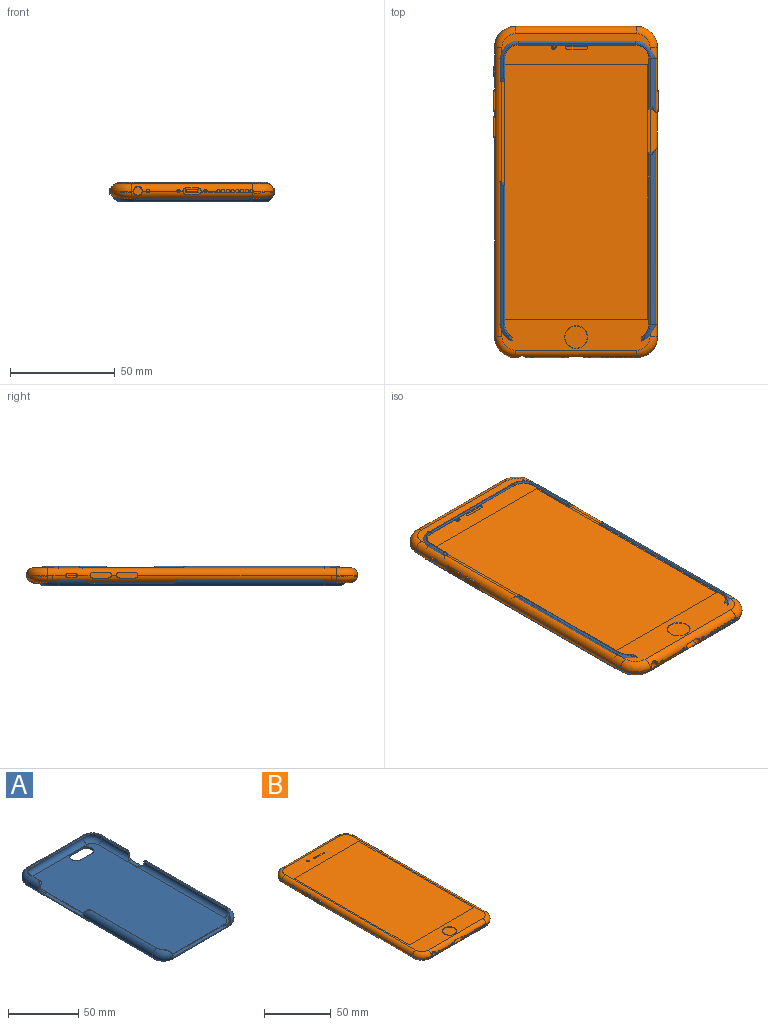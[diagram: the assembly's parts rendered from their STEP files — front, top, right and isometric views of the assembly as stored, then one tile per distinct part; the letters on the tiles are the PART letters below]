
ASSEMBLY  parts=2 mates=1
PART A: 91 faces, bbox 79x150.1x9.5 mm
  f0: cylinder r=3.5mm len=127.1mm, axis (0,1,0), area 1149.3mm2, adj f1,f8,f14,f16,f26,f53,f54,f55
  f1: cylinder r=0.5mm len=82.87mm, axis (0,1,0), area 128mm2, adj f0,f9,f15,f59,f60
  f2: cylinder r=3.5mm len=127.1mm, axis (0,1,0), area 873.9mm2, adj f3,f5,f11,f22,f26,f27,f28,f42
  f3: cylinder r=0.5mm len=11.42mm, axis (0,1,0), area 15.6mm2, adj f2,f4,f23,f46,f51
  f4: cylinder r=5mm len=127.1mm, axis (0,1,0), area 1097.8mm2, adj f3,f13,f24,f25,f27,f51,f52,f84
  f5: plane 16.43x0mm, normal (1,0,0), area 0.1mm2, adj f2,f26,f42
  f6: cylinder r=3.5mm len=56mm, axis (1,0,0), area 26.2mm2, adj f8,f11,f26,f31,f34,f35,f40,f41
  f7: cylinder r=5mm len=56mm, axis (1,0,0), area 114.5mm2, adj f10,f13,f25,f71,f72,f73
  f8: torus R=5.74mm, axis (0,0,1), area 122.4mm2, adj f0,f6,f9,f26,f29,f30,f31
  f9: torus R=6.88mm, axis (0,0,1), area 10.2mm2, adj f1,f8,f10,f29,f32,f33
  f10: torus R=5.6mm, axis (0,0,1), area 165.3mm2, adj f7,f9,f15,f25,f32,f74,f75,f76
  f11: torus R=5.74mm, axis (0,0,1), area 122.4mm2, adj f2,f6,f12,f26,f35,f36,f37
  f12: torus R=6.88mm, axis (0,0,1), area 10.2mm2, adj f11,f13,f27,f37,f38,f39
  f13: torus R=5.6mm, axis (0,0,1), area 165.3mm2, adj f4,f7,f12,f25,f38,f68,f69,f70
  f14: cylinder r=0.5mm len=24.73mm, axis (0,1,0), area 36.6mm2, adj f0,f15,f17,f53,f61
  f15: cylinder r=5mm len=127.1mm, axis (0,1,0), area 1384.9mm2, adj f1,f10,f14,f18,f25,f60,f61,f77
  f16: torus R=5.74mm, axis (0,0,1), area 129.9mm2, adj f0,f17,f19,f26
  f17: torus R=6.88mm, axis (0,0,1), area 16.2mm2, adj f14,f16,f18,f20
  f18: torus R=5.6mm, axis (0,0,1), area 182mm2, adj f15,f17,f21,f25
  f19: cylinder r=3.5mm len=56mm, axis (-1,0,0), area 572.6mm2, adj f16,f20,f22,f26,f64
  f20: cylinder r=0.5mm len=56mm, axis (-1,0,0), area 88mm2, adj f17,f19,f21,f23
  f21: cylinder r=5mm len=56mm, axis (-1,0,0), area 688.9mm2, adj f18,f20,f24,f25
  f22: torus R=5.74mm, axis (0,0,1), area 129.9mm2, adj f2,f19,f23,f26
  f23: torus R=6.88mm, axis (0,0,1), area 16.2mm2, adj f3,f20,f22,f24
  f24: torus R=5.6mm, axis (0,0,1), area 182mm2, adj f4,f21,f23,f25
  f25: plane 142.1x71mm, normal (0,0,-1), area 9861.1mm2, adj f4,f7,f10,f13,f15,f18,f21,f24
  f26: plane 138.18x67.14mm, normal (0,0,1), area 9053.4mm2, adj f0,f2,f5,f6,f8,f11,f16,f19
  f27: cylinder r=0.5mm len=68.7mm, axis (0,1,0), area 105.6mm2, adj f2,f4,f12,f47,f52
  f28: plane 73.67x0mm, normal (1,0,0), area 0.3mm2, adj f2,f26,f43
  f29: cylinder r=3.5mm len=4.97mm, axis (0,1,0), area 7.4mm2, adj f8,f9,f30,f32,f33,f76
  f30: plane 1.06x0.55mm, normal (-1,0,0), area 0.5mm2, adj f8,f29,f31,f75
  f31: cylinder r=3.5mm len=4.29mm, axis (0,1,0), area 9.6mm2, adj f6,f8,f30,f34,f73,f74
  f32: plane 1.34x0.37mm, normal (-1,0,0), area 0.2mm2, adj f9,f10,f29,f33,f76
  f33: plane 0.66x0.4mm, normal (0,-1,0), area 0.1mm2, adj f9,f29,f32
  f34: plane 50.8x3.01mm, normal (0,0,1), area 152.9mm2, adj f6,f31,f35,f72
  f35: cylinder r=3.5mm len=4.29mm, axis (0,1,0), area 9.6mm2, adj f6,f11,f34,f36,f70,f71
  f36: plane 1.06x0.55mm, normal (1,0,0), area 0.5mm2, adj f11,f35,f37,f69
  f37: cylinder r=3.5mm len=4.97mm, axis (0,1,0), area 7.4mm2, adj f11,f12,f36,f38,f39,f68
  f38: plane 1.34x0.37mm, normal (1,0,0), area 0.2mm2, adj f12,f13,f37,f39,f68
  f39: plane 0.66x0.4mm, normal (0,-1,0), area 0.1mm2, adj f12,f37,f38
  f40: cylinder r=3.5mm len=0.17mm, axis (0,1,0), area 0mm2, adj f6,f26
  f41: cylinder r=3.5mm len=0.17mm, axis (0,1,0), area 0mm2, adj f6,f26
  f42: cylinder r=3.5mm len=0.17mm, axis (-1,0,0), area 0mm2, adj f2,f5,f26
  f43: cylinder r=3.5mm len=0.17mm, axis (-1,0,0), area 0mm2, adj f2,f26,f28
  f44: plane 37x3.01mm, normal (0,0,1), area 111.4mm2, adj f2,f49,f50,f87
  f45: plane 1.06x0.47mm, normal (0,-1,0), area 0.5mm2, adj f2,f46,f49,f89
  f46: cylinder r=3.5mm len=3.8mm, axis (-1,0,0), area 8.6mm2, adj f2,f3,f45,f51,f90
  f47: cylinder r=3.5mm len=3.8mm, axis (-1,0,0), area 8.6mm2, adj f2,f27,f48,f52,f84
  f48: plane 1.09x0.97mm, normal (0,1,0), area 1mm2, adj f2,f47,f50,f85
  f49: cylinder r=3.5mm len=4.36mm, axis (-1,0,0), area 8.9mm2, adj f2,f44,f45,f88
  f50: cylinder r=3.5mm len=4.38mm, axis (-1,0,0), area 10.2mm2, adj f2,f44,f48,f86
  f51: plane 1.53x0.39mm, normal (0,-1,0), area 0.3mm2, adj f3,f4,f46,f90
  f52: plane 1.53x0.39mm, normal (0,1,0), area 0.3mm2, adj f4,f27,f47,f84
  f53: cylinder r=3.5mm len=3.85mm, axis (1,0,0), area 9mm2, adj f0,f14,f54,f61,f77
  f54: plane 1.05x0.32mm, normal (0,-1,0), area 0.3mm2, adj f0,f53,f55,f78
  f55: cylinder r=3.5mm len=4.36mm, axis (1,0,0), area 8.9mm2, adj f0,f54,f56,f79
  f56: plane 9x3.01mm, normal (0,0,1), area 27.1mm2, adj f0,f55,f57,f80
  f57: cylinder r=3.5mm len=4.36mm, axis (1,0,0), area 8.9mm2, adj f0,f56,f58,f81
  f58: plane 1.05x0.32mm, normal (0,1,0), area 0.3mm2, adj f0,f57,f59,f82
  f59: cylinder r=3.5mm len=3.85mm, axis (1,0,0), area 9mm2, adj f0,f1,f58,f60,f83
  f60: plane 1.84x0.56mm, normal (0,1,0), area 0.6mm2, adj f1,f15,f59,f83
  f61: plane 1.84x0.56mm, normal (0,-1,0), area 0.6mm2, adj f14,f15,f53,f77
  f62: cylinder r=3.5mm len=0.17mm, axis (1,0,0), area 0mm2, adj f0,f26
  f63: cylinder r=3.5mm len=0.17mm, axis (1,0,0), area 0mm2, adj f0,f26
  f64: plane 10.12x1.61mm, normal (0,-1,0), area 16.2mm2, adj f19,f25,f65,f67
  f65: cylinder r=5mm len=10mm, axis (0,0,1), area 25.1mm2, adj f25,f26,f64,f66
  f66: plane 10.11x1.6mm, normal (0,1,0), area 16.2mm2, adj f25,f26,f65,f67
  f67: cylinder r=5mm len=10mm, axis (0,0,1), area 25.1mm2, adj f25,f26,f64,f66
  f68: bspline ~4.29x3.86mm, area 2.1mm2, adj f13,f37,f38,f69
  f69: bspline ~0.6x0.38mm, area 0.2mm2, adj f13,f36,f68,f70
  f70: bspline ~2.94x1.44mm, area 1.4mm2, adj f13,f35,f69,f71
  f71: bspline ~2.6x1.46mm, area 1.5mm2, adj f7,f35,f70,f72
  f72: plane 50.8x0.51mm, normal (0,-0.92,0.38), area 28mm2, adj f7,f34,f71,f73
  f73: bspline ~2.6x1.46mm, area 1.5mm2, adj f7,f31,f72,f74
  f74: bspline ~2.94x1.45mm, area 1.4mm2, adj f10,f31,f73,f75
  f75: bspline ~0.6x0.38mm, area 0.2mm2, adj f10,f30,f74,f76
  f76: bspline ~4.29x3.86mm, area 2.1mm2, adj f10,f29,f32,f75
  f77: bspline ~3.8x3.54mm, area 1.8mm2, adj f15,f53,f61,f78
  f78: cone r=4.7mm half-angle=45deg, axis (0,1,0), area 0.1mm2, adj f15,f54,f77,f79
  f79: bspline ~4.04x3.8mm, area 2.9mm2, adj f15,f55,f78,f80
  f80: plane 9x0.51mm, normal (0.92,0,0.38), area 5mm2, adj f15,f56,f79,f81
  f81: bspline ~4.04x3.8mm, area 2.9mm2, adj f15,f57,f80,f82
  f82: cone r=4.7mm half-angle=45deg, axis (0,-1,0), area 0.1mm2, adj f15,f58,f81,f83
  f83: bspline ~3.5x3.5mm, area 1.8mm2, adj f15,f59,f60,f82
  f84: bspline ~3.81x3.54mm, area 1.7mm2, adj f4,f47,f52,f85
  f85: cone r=5mm half-angle=45deg, axis (0,-1,0), area 0.4mm2, adj f4,f48,f84,f86
  f86: bspline ~3.79x3.79mm, area 2.7mm2, adj f4,f50,f85,f87
  f87: plane 37x0.51mm, normal (-0.92,0,0.38), area 20.4mm2, adj f4,f44,f86,f88
  f88: bspline ~4.04x3.8mm, area 2.9mm2, adj f4,f49,f87,f89
  f89: cone r=5mm half-angle=45deg, axis (0,1,0), area 0.2mm2, adj f4,f45,f88,f90
  f90: bspline ~3.81x3.54mm, area 1.7mm2, adj f4,f46,f51,f89
PART B: 184 faces, bbox 79.4x159.7x7.8 mm
  f0: cylinder r=3.55mm len=3.55mm, axis (0,1,0), area 12.2mm2, adj f2,f5,f6,f32,f62
  f1: cylinder r=3.55mm len=3.55mm, axis (0,-1,0), area 12.2mm2, adj f2,f4,f7,f36,f59
  f2: plane 70.69x1.5mm, normal (0,0,-1), area 106mm2, adj f0,f1,f8,f39
  f3: cylinder r=3.55mm len=57.79mm, axis (-1,0,0), area 154.9mm2, adj f4,f5,f9,f10,f11,f12,f13,f14
  f4: torus R=6.45mm, axis (0,0,-1), area 41.5mm2, adj f1,f3,f22,f23,f49,f50
  f5: torus R=6.45mm, axis (0,0,-1), area 42.1mm2, adj f0,f3,f24,f25,f69
  f6: cylinder r=3.55mm len=132.83mm, axis (0,1,0), area 710.8mm2, adj f0,f8,f28,f62,f78,f79,f81,f83
  f7: cylinder r=3.55mm len=132.83mm, axis (0,-1,0), area 709.9mm2, adj f1,f8,f27,f59,f74,f99,f100,f101
  f8: plane 132.83x70.69mm, normal (0,0,-1), area 9132.5mm2, adj f2,f6,f7,f26,f48,f65
  f9: cylinder r=3.55mm len=0.95mm, axis (-1,0,0), area 0.1mm2, adj f3,f43,f148
  f10: cylinder r=3.55mm len=2mm, axis (-1,0,0), area 0.4mm2, adj f3,f43,f56,f148
  f11: cylinder r=3.55mm len=13.09mm, axis (-1,0,0), area 4.2mm2, adj f3,f40,f43,f56
  f12: cylinder r=3.55mm len=1.41mm, axis (-1,0,0), area 0.5mm2, adj f3,f40,f43,f109
  f13: cylinder r=3.55mm len=1.49mm, axis (-1,0,0), area 0.7mm2, adj f3,f43,f44,f111
  f14: cylinder r=3.55mm len=5.01mm, axis (-1,0,0), area 2.5mm2, adj f3,f43,f44,f131
  f15: cylinder r=3.55mm len=1.06mm, axis (-1,0,0), area 0.5mm2, adj f3,f43,f129,f131
  f16: cylinder r=3.55mm len=1.09mm, axis (-1,0,0), area 0.5mm2, adj f3,f43,f127,f129
  f17: cylinder r=3.55mm len=1.12mm, axis (-1,0,0), area 0.5mm2, adj f3,f43,f125,f127
  f18: cylinder r=3.55mm len=1.14mm, axis (-1,0,0), area 0.5mm2, adj f3,f43,f123,f125
  f19: cylinder r=3.55mm len=1.17mm, axis (-1,0,0), area 0.5mm2, adj f3,f43,f121,f123
  f20: cylinder r=3.55mm len=1.2mm, axis (-1,0,0), area 0.6mm2, adj f3,f43,f119,f121
  f21: cylinder r=3.55mm len=1.23mm, axis (-1,0,0), area 0.6mm2, adj f3,f43,f117,f119
  f22: torus R=6.45mm, axis (0,0,-1), area 4.3mm2, adj f4,f50
  f23: torus R=6.45mm, axis (0,0,-1), area 5.8mm2, adj f4,f50,f117
  f24: torus R=6.45mm, axis (0,0,-1), area 4.7mm2, adj f5,f72
  f25: torus R=6.45mm, axis (0,0,-1), area 4.7mm2, adj f5,f72
  f26: plane 70.69x1.5mm, normal (0,0,-1), area 106mm2, adj f8,f27,f28,f47
  f27: cylinder r=3.55mm len=3.55mm, axis (0,-1,0), area 12.2mm2, adj f7,f26,f31,f58,f59
  f28: cylinder r=3.55mm len=3.55mm, axis (0,1,0), area 12.1mm2, adj f6,f26,f29,f33,f61,f62
  f29: torus R=6.45mm, axis (0,0,-1), area 42.4mm2, adj f28,f30,f34,f35,f66,f67
  f30: cylinder r=3.55mm len=57.79mm, axis (1,0,0), area 196mm2, adj f29,f31,f68,f70
  f31: torus R=6.45mm, axis (0,0,-1), area 42.1mm2, adj f27,f30,f37,f38,f71
  f32: cylinder r=3.55mm len=2.05mm, axis (0,1,0), area 2.4mm2, adj f0,f39,f69
  f33: cylinder r=3.55mm len=0.28mm, axis (0,1,0), area 0mm2, adj f28,f34,f62
  f34: torus R=6.45mm, axis (0,0,-1), area 3.4mm2, adj f29,f33,f67
  f35: torus R=6.45mm, axis (0,0,-1), area 5.7mm2, adj f29,f67
  f36: cylinder r=3.55mm len=2.05mm, axis (0,-1,0), area 2.4mm2, adj f1,f39,f49
  f37: torus R=6.45mm, axis (0,0,-1), area 4.7mm2, adj f31,f73
  f38: torus R=6.45mm, axis (0,0,-1), area 4.7mm2, adj f31,f73
  f39: plane 70.69x7.57mm, normal (0,0,-1), area 517.3mm2, adj f2,f32,f36,f42,f49,f69
  f40: cylinder r=3.55mm len=1.6mm, axis (-1,0,0), area 0.8mm2, adj f3,f11,f12,f41,f168,f169,f170,f171
  f41: cylinder r=3.55mm len=1.6mm, axis (1,0,0), area 0.9mm2, adj f40,f43,f163,f164,f165,f166,f167,f168
  f42: cylinder r=3.55mm len=57.79mm, axis (-1,0,0), area 124.3mm2, adj f3,f39,f49,f69
  f43: cylinder r=3.55mm len=57.79mm, axis (1,0,0), area 290.7mm2, adj f9,f10,f11,f12,f13,f14,f15,f16
  f44: cylinder r=3.55mm len=1.6mm, axis (-1,0,0), area 0.8mm2, adj f3,f13,f14,f45,f153,f154,f155,f156
  f45: cylinder r=3.55mm len=1.6mm, axis (1,0,0), area 0.9mm2, adj f43,f44,f150,f151,f152,f153,f159,f160
  f46: plane 1.5x1.5mm, normal (0,0,1), area 1mm2, adj f142,f143
  f47: plane 70.69x7.57mm, normal (0,0,-1), area 456.1mm2, adj f26,f58,f61,f66,f68,f71,f104,f144
  f48: plane 18.21x17.51mm, normal (0,0,-1), area 242.8mm2, adj f8
  f49: torus R=6.45mm, axis (0,0,-1), area 24.6mm2, adj f4,f36,f39,f42
  f50: torus R=6.45mm, axis (0,0,-1), area 76.2mm2, adj f4,f22,f23,f43,f59,f63,f117
  f51: cylinder r=1.7mm len=1.7mm, axis (0,0,-1), area 1.5mm2, adj f52,f54,f113
  f52: cylinder r=1.7mm len=6.5mm, axis (1,0,0), area 10.1mm2, adj f51,f53,f54,f114
  f53: cylinder r=1.7mm len=1.7mm, axis (0,0,1), area 1.5mm2, adj f52,f54,f115
  f54: cylinder r=1.7mm len=6.5mm, axis (-1,0,0), area 10.1mm2, adj f51,f52,f53,f116
  f55: plane 8.7x2.95mm, normal (0,-1,0), area 12.7mm2, adj f109,f110,f111,f112,f113,f114,f115,f116
  f56: cylinder r=3.55mm len=1.6mm, axis (-1,0,0), area 1mm2, adj f3,f10,f11,f57
  f57: cylinder r=3.55mm len=1.6mm, axis (1,0,0), area 1mm2, adj f43,f56
  f58: cylinder r=3.55mm len=2.05mm, axis (0,-1,0), area 2.4mm2, adj f27,f47,f71
  f59: cylinder r=3.55mm len=138.07mm, axis (0,1,0), area 739.1mm2, adj f1,f7,f27,f50,f63,f73,f75,f98
  f60: plane 5.61x1.96mm, normal (-1,0,0), area 5.5mm2, adj f88,f89,f90,f91,f92,f93,f94,f95
  f61: cylinder r=3.55mm len=2.09mm, axis (0,1,0), area 2.5mm2, adj f28,f47,f66
  f62: cylinder r=3.55mm len=138.07mm, axis (0,-1,0), area 737.2mm2, adj f0,f6,f28,f33,f63,f67,f72,f79
  f63: plane 150.97x70.69mm, normal (0,0,1), area 2217.1mm2, adj f43,f50,f59,f62,f64,f67,f70,f72
  f64: plane 121.54x68.36mm, normal (0,0,1), area 8308.5mm2, adj f63
  f65: plane 5.18x4.88mm, normal (0,0,-1), area 13.6mm2, adj f8
  f66: torus R=6.45mm, axis (0,0,-1), area 24.8mm2, adj f29,f47,f61,f68
  f67: torus R=6.45mm, axis (0,0,-1), area 76.3mm2, adj f29,f34,f35,f62,f63,f70
  f68: cylinder r=3.55mm len=57.79mm, axis (1,0,0), area 126.3mm2, adj f30,f47,f66,f71,f106
  f69: torus R=6.45mm, axis (0,0,-1), area 24.8mm2, adj f5,f32,f39,f42
  f70: cylinder r=3.55mm len=57.79mm, axis (-1,0,0), area 322.3mm2, adj f30,f63,f67,f73
  f71: torus R=6.45mm, axis (0,0,-1), area 24.8mm2, adj f31,f47,f58,f68
  f72: torus R=6.45mm, axis (0,0,-1), area 76.3mm2, adj f24,f25,f43,f62,f63
  f73: torus R=6.45mm, axis (0,0,-1), area 76.3mm2, adj f37,f38,f59,f63,f70
  f74: cylinder r=3.55mm len=15.81mm, axis (0,-1,0), area 17.2mm2, adj f7,f75,f102
  f75: cylinder r=3.55mm len=15.81mm, axis (0,1,0), area 16.6mm2, adj f59,f74,f102
  f76: cone r=5.45mm half-angle=45deg, axis (0,0,1), area 7.2mm2, adj f63,f77
  f77: plane 10.6x10.6mm, normal (0,0,1), area 88.2mm2, adj f76
  f78: plane 7.4x0.59mm, normal (0,0,-1), area 4.3mm2, adj f6,f79,f81,f82
  f79: cylinder r=1.4mm len=2.8mm, axis (-1,0,0), area 2mm2, adj f6,f62,f78,f80,f82
  f80: plane 7.4x0.59mm, normal (0,0,1), area 4.3mm2, adj f62,f79,f81,f82
  f81: cylinder r=1.4mm len=2.8mm, axis (-1,0,0), area 2mm2, adj f6,f62,f78,f80,f82
  f82: plane 10.2x2.8mm, normal (-1,0,0), area 26.9mm2, adj f78,f79,f80,f81
  f83: plane 7.4x0.59mm, normal (0,0,-1), area 4.3mm2, adj f6,f84,f86,f87
  f84: cylinder r=1.4mm len=2.8mm, axis (-1,0,0), area 2mm2, adj f6,f62,f83,f85,f87
  f85: plane 7.4x0.59mm, normal (0,0,1), area 4.3mm2, adj f62,f84,f86,f87
  f86: cylinder r=1.4mm len=2.8mm, axis (-1,0,0), area 2mm2, adj f6,f62,f83,f85,f87
  f87: plane 10.2x2.8mm, normal (-1,0,0), area 26.9mm2, adj f83,f84,f85,f86
  f88: cylinder r=0.98mm len=1.96mm, axis (-1,0,0), area 1.3mm2, adj f6,f60,f62,f89,f91
  f89: plane 3.65x0.36mm, normal (0,0,-1), area 1.3mm2, adj f60,f62,f88,f90
  f90: cylinder r=0.98mm len=1.96mm, axis (-1,0,0), area 1.3mm2, adj f6,f60,f62,f89,f91
  f91: plane 3.65x0.36mm, normal (0,0,1), area 1.3mm2, adj f6,f60,f88,f90
  f92: cylinder r=0.47mm len=0.93mm, axis (1,0,0), area 1.2mm2, adj f60,f93,f95,f96
  f93: plane 4.31x0.8mm, normal (0,0,-1), area 3.4mm2, adj f60,f92,f94,f96
  f94: cylinder r=0.47mm len=0.93mm, axis (1,0,0), area 1.2mm2, adj f60,f93,f95,f96
  f95: plane 4.31x0.8mm, normal (0,0,1), area 3.4mm2, adj f60,f92,f94,f96
  f96: plane 5.24x0.93mm, normal (-1,0,0), area 4.7mm2, adj f92,f93,f94,f95
  f97: plane 10.2x2.8mm, normal (1,0,0), area 26.9mm2, adj f98,f99,f100,f101
  f98: plane 7.4x0.59mm, normal (0,0,1), area 4.3mm2, adj f59,f97,f99,f101
  f99: cylinder r=1.4mm len=2.8mm, axis (1,0,0), area 2mm2, adj f7,f59,f97,f98,f100
  f100: plane 7.4x0.59mm, normal (0,0,-1), area 4.3mm2, adj f7,f97,f99,f101
  f101: cylinder r=1.4mm len=2.8mm, axis (1,0,0), area 2mm2, adj f7,f59,f97,f98,f100
  f102: cylinder r=1mm len=2mm, axis (1,0,0), area 7.3mm2, adj f74,f75,f103
  f103: plane 2x2mm, normal (1,0,0), area 3.1mm2, adj f102
  f104: cylinder r=3.83mm len=7.66mm, axis (0,0,1), area 16.1mm2, adj f47,f105,f106
  f105: plane 7.66x7.66mm, normal (0,0,-1), area 46.1mm2, adj f104
  f106: plane 2.32x0.18mm, normal (0,0,1), area 0.3mm2, adj f68,f104
  f107: cylinder r=2.02mm len=9.64mm, axis (0,-1,0), area 117.8mm2, adj f108,f148,f149
  f108: plane 4.05x4.05mm, normal (0,-1,0), area 12.9mm2, adj f107
  f109: cylinder r=1.47mm len=5mm, axis (0,-1,0), area 22.5mm2, adj f3,f12,f43,f55,f110,f112
  f110: plane 5.75x4.68mm, normal (0,0,-1), area 26.9mm2, adj f43,f55,f109,f111
  f111: cylinder r=1.47mm len=5mm, axis (0,-1,0), area 22.5mm2, adj f3,f13,f43,f55,f110,f112
  f112: plane 5.75x4.68mm, normal (0,0,1), area 26.9mm2, adj f3,f55,f109,f111
  f113: plane 1.7x0.8mm, normal (1,0,0), area 1.4mm2, adj f51,f55,f114,f116
  f114: plane 6.5x0.8mm, normal (0,0,1), area 5.2mm2, adj f52,f55,f113,f115
  f115: plane 1.7x0.8mm, normal (-1,0,0), area 1.4mm2, adj f53,f55,f114,f116
  f116: plane 6.5x0.8mm, normal (0,0,-1), area 5.2mm2, adj f54,f55,f113,f115
  f117: cylinder r=0.8mm len=1.6mm, axis (0,-1,0), area 4.9mm2, adj f3,f21,f23,f43,f50,f118
  f118: plane 1.6x1.6mm, normal (0,-1,0), area 2mm2, adj f117
  f119: cylinder r=0.8mm len=1.6mm, axis (0,-1,0), area 4.9mm2, adj f3,f20,f21,f43,f120
  f120: plane 1.6x1.6mm, normal (0,-1,0), area 2mm2, adj f119
  f121: cylinder r=0.8mm len=1.6mm, axis (0,-1,0), area 4.9mm2, adj f3,f19,f20,f43,f122
  f122: plane 1.6x1.6mm, normal (0,-1,0), area 2mm2, adj f121
  f123: cylinder r=0.8mm len=1.6mm, axis (0,-1,0), area 4.9mm2, adj f3,f18,f19,f43,f124
  f124: plane 1.6x1.6mm, normal (0,-1,0), area 2mm2, adj f123
  f125: cylinder r=0.8mm len=1.6mm, axis (0,-1,0), area 4.9mm2, adj f3,f17,f18,f43,f126
  f126: plane 1.6x1.6mm, normal (0,-1,0), area 2mm2, adj f125
  f127: cylinder r=0.8mm len=1.6mm, axis (0,-1,0), area 4.9mm2, adj f3,f16,f17,f43,f128
  f128: plane 1.6x1.6mm, normal (0,-1,0), area 2mm2, adj f127
  f129: cylinder r=0.8mm len=1.6mm, axis (0,-1,0), area 4.9mm2, adj f3,f15,f16,f43,f130
  f130: plane 1.6x1.6mm, normal (0,-1,0), area 2mm2, adj f129
  f131: cylinder r=0.8mm len=1.6mm, axis (0,-1,0), area 4.9mm2, adj f3,f14,f15,f43,f132
  f132: plane 1.6x1.6mm, normal (0,-1,0), area 2mm2, adj f131
  f133: cylinder r=0.6mm len=1.2mm, axis (0,0,1), area 0.2mm2, adj f63,f134,f136,f137
  f134: plane 9.5x0.1mm, normal (0,-1,0), area 1mm2, adj f63,f133,f135,f137
  f135: cylinder r=0.6mm len=1.2mm, axis (0,0,1), area 0.2mm2, adj f63,f134,f136,f137
  f136: plane 9.5x0.1mm, normal (0,1,0), area 1mm2, adj f63,f133,f135,f137
  f137: plane 10.7x1.2mm, normal (0,0,1), area 12.5mm2, adj f133,f134,f135,f136
  f138: cylinder r=1.25mm len=2.5mm, axis (0,0,1), area 2mm2, adj f63,f139
  f139: plane 2.5x2.5mm, normal (0,0,1), area 1.8mm2, adj f138,f140
  f140: cylinder r=1mm len=2mm, axis (0,0,1), area 1.6mm2, adj f139,f141
  f141: plane 2x2mm, normal (0,0,1), area 1.4mm2, adj f140,f142
  f142: cylinder r=0.75mm len=1.5mm, axis (0,0,1), area 1.2mm2, adj f46,f141
  f143: sphere r=0.5mm, area 1.6mm2, adj f46
  f144: cylinder r=2.06mm len=4.11mm, axis (0,0,1), area 0.6mm2, adj f47,f145
  f145: plane 4.11x4.11mm, normal (0,0,-1), area 13.3mm2, adj f144
  f146: cylinder r=0.8mm len=1.6mm, axis (0,0,-1), area 0.5mm2, adj f47,f147
  f147: plane 1.6x1.6mm, normal (0,0,-1), area 2mm2, adj f146
  f148: bspline ~4.23x2.35mm, area 2.8mm2, adj f3,f9,f10,f107,f149
  f149: bspline ~4.23x2.35mm, area 2.8mm2, adj f43,f107,f148
  f150: plane 0.2x0.17mm, normal (0,0,-1), area 0mm2, adj f45,f151,f161,f162
  f151: plane 0.35x0.2mm, normal (-1,0,0), area 0.1mm2, adj f45,f150,f152,f162
  f152: plane 0.35x0.2mm, normal (0,0,-1), area 0.1mm2, adj f45,f151,f153,f162
  f153: plane 0.2x0.2mm, normal (-1,0,0), area 0mm2, adj f44,f45,f152,f154,f162
  f154: plane 0.35x0.2mm, normal (0,0,1), area 0.1mm2, adj f44,f153,f155,f162
  f155: plane 0.35x0.2mm, normal (-1,0,0), area 0.1mm2, adj f44,f154,f156,f162
  f156: plane 0.2x0.17mm, normal (0,0,1), area 0mm2, adj f44,f155,f157,f162
  f157: plane 0.35x0.2mm, normal (1,0,0), area 0.1mm2, adj f44,f156,f158,f162
  f158: plane 0.35x0.2mm, normal (0,0,1), area 0.1mm2, adj f44,f157,f159,f162
  f159: plane 0.2x0.2mm, normal (1,0,0), area 0mm2, adj f44,f45,f158,f160,f162
  f160: plane 0.35x0.2mm, normal (0,0,-1), area 0.1mm2, adj f45,f159,f161,f162
  f161: plane 0.35x0.2mm, normal (1,0,0), area 0.1mm2, adj f45,f150,f160,f162
  f162: plane 0.9x0.9mm, normal (0,-1,0), area 0.3mm2, adj f150,f151,f152,f153,f154,f155,f156,f157
  f163: plane 0.35x0.2mm, normal (0,0,-1), area 0.1mm2, adj f41,f164,f174,f175
  f164: plane 0.35x0.2mm, normal (-1,0,0), area 0.1mm2, adj f41,f163,f165,f175
  f165: plane 0.2x0.17mm, normal (0,0,-1), area 0mm2, adj f41,f164,f166,f175
  f166: plane 0.35x0.2mm, normal (1,0,0), area 0.1mm2, adj f41,f165,f167,f175
  f167: plane 0.35x0.2mm, normal (0,0,-1), area 0.1mm2, adj f41,f166,f168,f175
  f168: plane 0.2x0.2mm, normal (1,0,0), area 0mm2, adj f40,f41,f167,f169,f175
  f169: plane 0.35x0.2mm, normal (0,0,1), area 0.1mm2, adj f40,f168,f170,f175
  f170: plane 0.35x0.2mm, normal (1,0,0), area 0.1mm2, adj f40,f169,f171,f175
  f171: plane 0.2x0.17mm, normal (0,0,1), area 0mm2, adj f40,f170,f172,f175
  f172: plane 0.35x0.2mm, normal (-1,0,0), area 0.1mm2, adj f40,f171,f173,f175
  f173: plane 0.35x0.2mm, normal (0,0,1), area 0.1mm2, adj f40,f172,f174,f175
  f174: plane 0.2x0.2mm, normal (-1,0,0), area 0mm2, adj f40,f41,f163,f173,f175
  f175: plane 0.9x0.9mm, normal (0,-1,0), area 0.3mm2, adj f163,f164,f165,f166,f167,f168,f169,f170
  f176: plane 6.9x6.9mm, normal (0,0,1), area 37.4mm2, adj f183
  f177: sphere r=1.52mm, area 4.8mm2, adj f178
  f178: cylinder r=1.12mm len=2.25mm, axis (0,0,-1), area 3.5mm2, adj f177,f179
  f179: plane 2.75x2.75mm, normal (0,0,-1), area 2mm2, adj f178,f180
  f180: plane 3.75x3.75mm, normal (0,0,-1), area 5.1mm2, adj f179,f181
  f181: cylinder r=1.88mm len=3.75mm, axis (0,0,-1), area 11.8mm2, adj f180,f182
  f182: plane 6.9x6.9mm, normal (0,0,-1), area 26.3mm2, adj f181,f183
  f183: cylinder r=3.45mm len=6.9mm, axis (0,0,-1), area 1.1mm2, adj f176,f182
PLACE A rot(axis=(0,0,1),0deg) t=(16.47,42.72,30.55)mm fixed
PLACE B rot(axis=(0,0,1),0deg) t=(16.1,42.58,30.55)mm
MATE slider B.f8 <-> A.f26  axis (0,0,-1) through (16.12,41.44,30.55)mm
